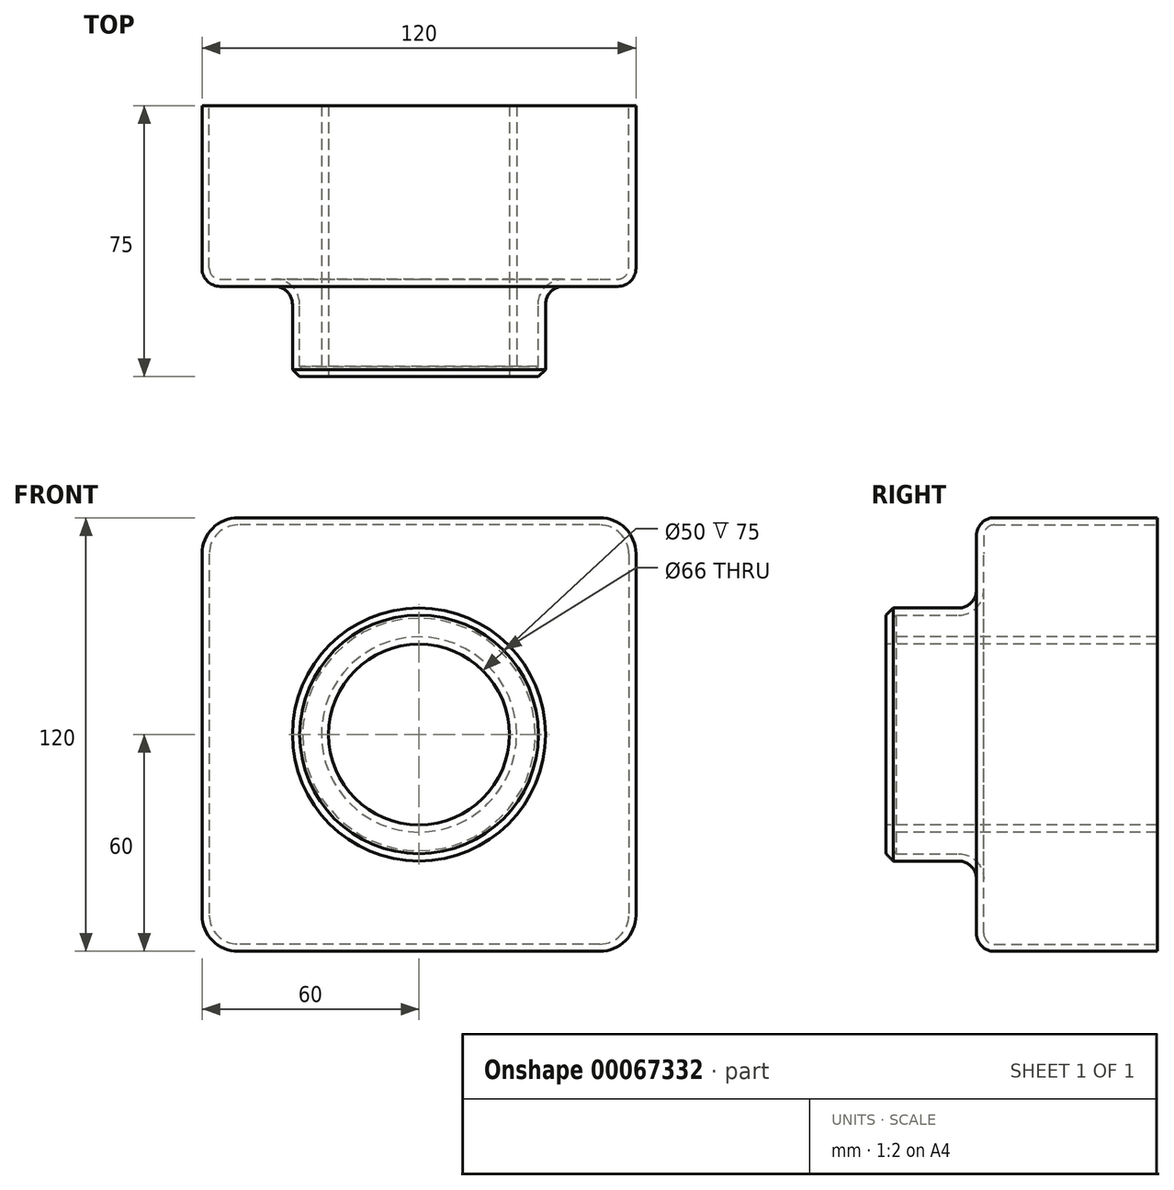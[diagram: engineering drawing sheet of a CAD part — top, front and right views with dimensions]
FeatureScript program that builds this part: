
annotation { "Feature Type Name" : "Feature", "Feature Type Description" : "" }
export const myFeature = defineFeature(function(context is Context, id is Id, definition is map)
    precondition{}
    {
        {
            var Q0;
            Q0=qCreatedBy(makeId("Front.planeOp"),FACE);
            var sketch = newSketch(context, id + "F0", { "sketchPlane" : qUnion([Q0])});
            skLineSegment(sketch, "E0.rect.bottom", {"start": v(60, 60) * mm, "end": v(-60, 60) * mm});
            skLineSegment(sketch, "E0.rect.top", {"start": v(60, -60) * mm, "end": v(-60, -60) * mm});
            skLineSegment(sketch, "E0.rect.left", {"start": v(60, 60) * mm, "end": v(60, -60) * mm});
            skLineSegment(sketch, "E0.rect.right", {"start": v(-60, 60) * mm, "end": v(-60, -60) * mm});
            skPoint(sketch, "E0.rect.middle", {"position": v(0, 0) * mm});
            skSolve(sketch);
        }
        {
            var Q0;
            Q0=makeQuery(id+"F0.imprint","IMPRINT",FACE,{"disambiguationData":[TD([[makeQuery(id+"F0.imprint","IMPRINT",EDGE,{"derivedFrom":sQuery(id+"F0.wireOp",EDGE,"E0.rect.bottom")}),1.0]])]});
            extrude(context, id + "F1", {"entities" : qUnion([Q0]), "depth" : 50 * mm});
        }
        {
            var Q0;
            Q0=makeQuery(id+"F1.opExtrude","CAP_FACE",FACE,{"disambiguationData":[OSD([sQuery(id+"F0.wireOp",EDGE,"E0.rect.bottom"),sQuery(id+"F0.wireOp",EDGE,"E0.rect.top"),sQuery(id+"F0.wireOp",EDGE,"E0.rect.left"),sQuery(id+"F0.wireOp",EDGE,"E0.rect.right")])],"isStart":false});
            var sketch = newSketch(context, id + "F2", { "sketchPlane" : qUnion([Q0])});
            skCircle(sketch, "E1", {"center": v(0, 0) * mm, "radius": 35 * mm});
            skSolve(sketch);
        }
        {
            var Q0;
            Q0 = qSketchRegion(id + "F2", true);
            extrude(context, id + "F3", {"entities" : qUnion([Q0]), "operationType" : NewBodyOperationType.ADD, "depth" : 25 * mm});
        }
        {
            var Q0;
            Q0=makeQuery(id+"F3.opExtrude","CAP_FACE",FACE,{"disambiguationData":[OSD([sQuery(id+"F2.wireOp",EDGE,"E1")])],"isStart":false});
            var sketch = newSketch(context, id + "F4", { "sketchPlane" : qUnion([Q0])});
            skCircle(sketch, "E2", {"center": v(0, 0) * mm, "radius": 25 * mm});
            skSolve(sketch);
        }
        {
            var Q0;
            Q0 = qSketchRegion(id + "F4", true);
            extrude(context, id + "F5", {"entities" : qUnion([Q0]), "operationType" : NewBodyOperationType.REMOVE, "endBound" : BoundingType.THROUGH_ALL, "oppositeDirection" : true, "depth" : 25 * mm});
        }
        {
            var Q0;
            Q0=makeQuery(id+"F1.opExtrude","SWEPT_EDGE",EDGE,{"disambiguationData":[OSD([sQuery(id+"F0.wireOp",EDGE,"E0.rect.bottom"),sQuery(id+"F0.wireOp",EDGE,"E0.rect.right")])]});
            var Q1;
            Q1=makeQuery(id+"F1.opExtrude","SWEPT_EDGE",EDGE,{"disambiguationData":[OSD([sQuery(id+"F0.wireOp",EDGE,"E0.rect.bottom"),sQuery(id+"F0.wireOp",EDGE,"E0.rect.left")])]});
            var Q2;
            Q2=makeQuery(id+"F1.opExtrude","SWEPT_EDGE",EDGE,{"disambiguationData":[OSD([sQuery(id+"F0.wireOp",EDGE,"E0.rect.top"),sQuery(id+"F0.wireOp",EDGE,"E0.rect.right")])]});
            var Q3;
            Q3=makeQuery(id+"F1.opExtrude","SWEPT_EDGE",EDGE,{"disambiguationData":[OSD([sQuery(id+"F0.wireOp",EDGE,"E0.rect.top"),sQuery(id+"F0.wireOp",EDGE,"E0.rect.left")])]});
            fillet(context, id + "F6", {"entities" : qUnion([Q0, Q1, Q2, Q3]), "radius" : 10 * mm, "tangentPropagation" : true, "allowEdgeOverflow" : false});
        }
        {
            var Q0;
            Q0=makeQuery(id+"F1.opExtrude","CAP_FACE",FACE,{"disambiguationData":[OSD([sQuery(id+"F0.wireOp",EDGE,"E0.rect.bottom"),sQuery(id+"F0.wireOp",EDGE,"E0.rect.top"),sQuery(id+"F0.wireOp",EDGE,"E0.rect.left"),sQuery(id+"F0.wireOp",EDGE,"E0.rect.right")])],"isStart":false});
            fillet(context, id + "F7", {"entities" : qUnion([Q0]), "radius" : 5 * mm, "tangentPropagation" : true, "allowEdgeOverflow" : false});
        }
        {
            var Q0;
            Q0=makeQuery(id+"F3.opExtrude","CAP_EDGE",EDGE,{"disambiguationData":[OSD([sQuery(id+"F2.wireOp",EDGE,"E1")])],"isStart":false});
            var Q1;
            Q1=makeQuery(id+"F5.boolean.opBoolean","COPY",EDGE,{"derivedFrom":makeQuery(id+"F5.opExtrude","CAP_EDGE",EDGE,{"disambiguationData":[OSD([sQuery(id+"F4.wireOp",EDGE,"E2")])],"isStart":true})});
            chamfer(context, id + "F8", {"entities" : qUnion([Q0, Q1]), "width" : 2 * mm, "tangentPropagation" : true});
        }
        {
            var Q0;
            Q0=makeQuery(id+"F1.opExtrude","CAP_FACE",FACE,{"disambiguationData":[OSD([sQuery(id+"F0.wireOp",EDGE,"E0.rect.bottom"),sQuery(id+"F0.wireOp",EDGE,"E0.rect.top"),sQuery(id+"F0.wireOp",EDGE,"E0.rect.left"),sQuery(id+"F0.wireOp",EDGE,"E0.rect.right")])],"isStart":true});
            shell(context, id + "F9", {"entities" : qUnion([Q0]), "thickness" : 2 * mm});
        }
    });
